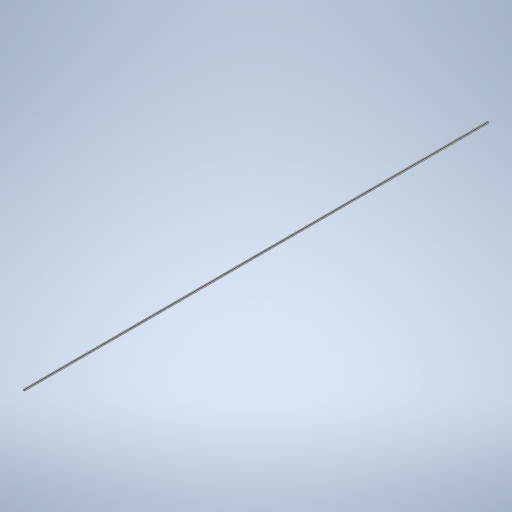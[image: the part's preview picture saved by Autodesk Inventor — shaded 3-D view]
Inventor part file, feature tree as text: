
AUTODESK INVENTOR PART (.ipt)
format: ipt  version: 2023 (Build 270158030, 158C)  size: 259,072 bytes
history: native  units: in
note: dims shown in document units (in); Inventor stores cm internally (conversion verified against a paired STEP export)
features: extrude x1, sketch x1
ambient origin geometry x8: Origin, YZ Plane, XZ Plane, XY Plane, X Axis, Y Axis, Z Axis, Center Point
bodies: Solid1 (feature_tree)
feature tree (2):
  extrude  "Extrusion1"  Depth=48.0in
  sketch  "Sketch1"  dims[d3=0.026in d4=0.0104in d5=1.1475in d6=0.0833in d7=0.0417in d9=0.0893in d10=0.01in d11=48.0in d12=0.0in]
